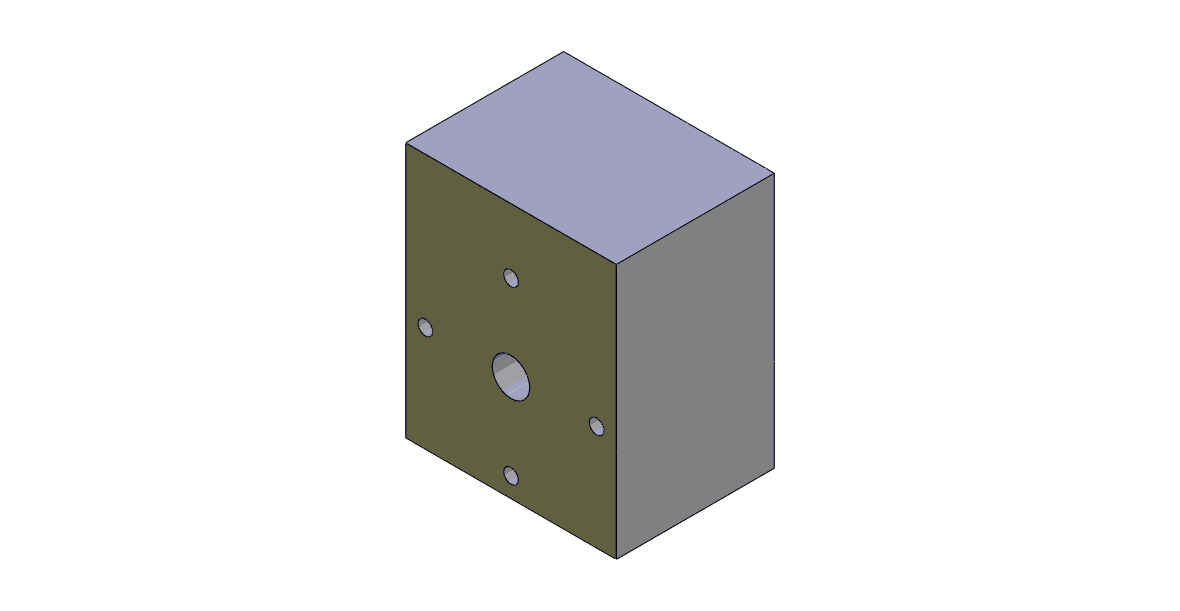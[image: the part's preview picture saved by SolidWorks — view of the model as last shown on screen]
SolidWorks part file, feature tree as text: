
SOLIDWORKS PART (.sldprt)
format: sldprt  version: not decoded by parser v0  size: 182,272 bytes
history: native  units: mm
features: sketch x5, hole x2, material x1, extrude x1 (+13 scaffold rows collapsed)
feature tree (22):
  scaffold x13  (default folders/planes/origin — collapsed)
  material  "Material <not specified>"
  sketch  "Sketch1"  dims[D1=97.0mm D2=80.0mm]
  extrude  "Boss-Extrude1"  Depth=60mm
  hole  "HOLE for 14 Centering Sleeve1"  Diameter=14.2mm Depth=60mm
  sketch  "Sketch5"  dims[D1=40.0mm]
  sketch  "Sketch6"  dims[hole-wizard template sketch: 59 standard entries collapsed; hole parameters kept: c18.Thru Hole Dia.=14.2mm c18.Thru Hole Depth=60.0mm]
  hole  "M5 Clearance Hole1"  Diameter=5.5mm Depth=60mm
  sketch  "Sketch8"  dims[D1=65.0mm D2=~4.288002mm]
  sketch  "Sketch7"  dims[hole-wizard template sketch: 60 standard entries collapsed; hole parameters kept: c18.Thru Hole Depth=60.0mm]
decode coverage: 8 of 8 modeling features carry decoded parameters
note: ~ marks probable driven/reference dimensions
note: suppression state not decoded; provenance and decode notes live in map.json
